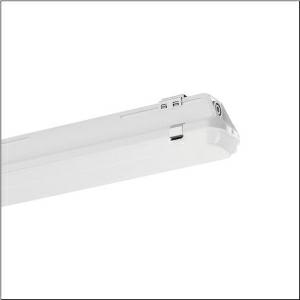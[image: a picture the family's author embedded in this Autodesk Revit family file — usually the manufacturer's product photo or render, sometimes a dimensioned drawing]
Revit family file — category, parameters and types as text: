
# Revit family: monsun_21_51fb20dl420k
name_source: partatom
category: Lighting Fixtures
units: mm (PartAtom-declared; Revit-internal decimal feet)

## family parameters
Cut with Voids When Loaded = No
Host = Face
Light Source = No
Part Type = Normal
Room Calculation Point = No
Round Connector Dimension = Use Diameter
Shared = No

## types (1)
- --- (1 x LED, 2660 lm, 17.1 W, 4000K)
    Apparent Load = 17 VA
    CIE Flux Codes = 45 75 93 94 100
    Color Rendering = 80
    Color Temperature = 4000K
    Default Elevation = 1800 mm
    Description = Monsun 21, damp-proof luminaire, chain hanger, primary optical cover: enclosure, of PC, light emission: direct distribution, primary light characteristic: symmetric, installation type: suspended mounting, surface-mounted, horizontal mounting, vertical mounting, LED, rated luminous flux: 2.660lm, luminous efficacy: 156lm/W, light colour: 840, colour temperature: 4000K, control gear: DALI 2, with terminal, 5-pole, max. 2.5mm², mains connection: 220..240V, AC, 50/60Hz, rated input power: 17W, housing, of glass-fibre reinforced plastic, uncoated, bright grey, incl. chain hanger, length: 1.299mm, width: 90mm, height: 88mm, clip for enclosure, of stainless steel (V2A), ceiling mounting element, of stainless steel (V2A), chain hanger, of stainless steel (V2A), protection rating (complete): IP66, insulation class (complete): insulation class I (protective earthing), certification: CE, ENEC, VDE, UKCA, protection symbol: D, impact resistance: IK08, permissible operating ambient temperature: -25..+35°C, standard: EN 50419, EN 60598-2-1, corresponds to IFS (International Featured Standards) requirements for safety and quality in the food industry, for indoor or canopied outdoor use, no direct snow, no direct sun, no direct rain, LABS conformity tested according to VDMA 24364:2018-05, contact your sales advisor before using the luminaires in applications with unclear chemical exposure, large temperature fluctuations or condensation-forming humidity, packaging unit: 1 piece
    Height = 88 mm
    Lamp = 1 x LED
    Lamp Light Flux = 2660 lm
    Lamp Power = 17.1 W
    Lamp count = 1
    Length = 1299 mm
    Luminous efficacy = 156 lm/W
    Manufacturer = Siteco
    ModVariant = No
    Model = 51FB20DL420K
    Mounting Place = Ceiling
    Mounting Type = Surface mounted
    Number of Poles = 1
    OnlyDefault = Yes
    Power Factor = 1
    Product Name = Monsun 21
    Product group = damp-proof luminaire
    ProductGroupID = 300
    Protection Class = Protection class I
    Protection Degree = IP 66
    RLX_Detail_Level = 1
    RLX_Emergency_Light_Flux = 0 lm
    RLX_Emergency_Type = 0
    RLX_Emergency_Type_DB = No
    RlxData = <blob elided: 93265 chars, md5=3c355817>
    Socket = socket
    Standby Power = 0 W
    System Light Flux = 2660 lm
    System Power = 17 W
    Type Comments = factory setting: luminous flux: 100 % | dim-lin: 254 | 110 mA
    Type Image = l_1319656.jpg
    URL = http://relux.com
    VarID = @adj_037139
    Voltage = 0 V
    Weight = 0.00 kg
    Width = 90 mm

## geometry (parser evidence)
native form markers: Blend x4, Sweep x13
no freeform markers — native parametric forms only
